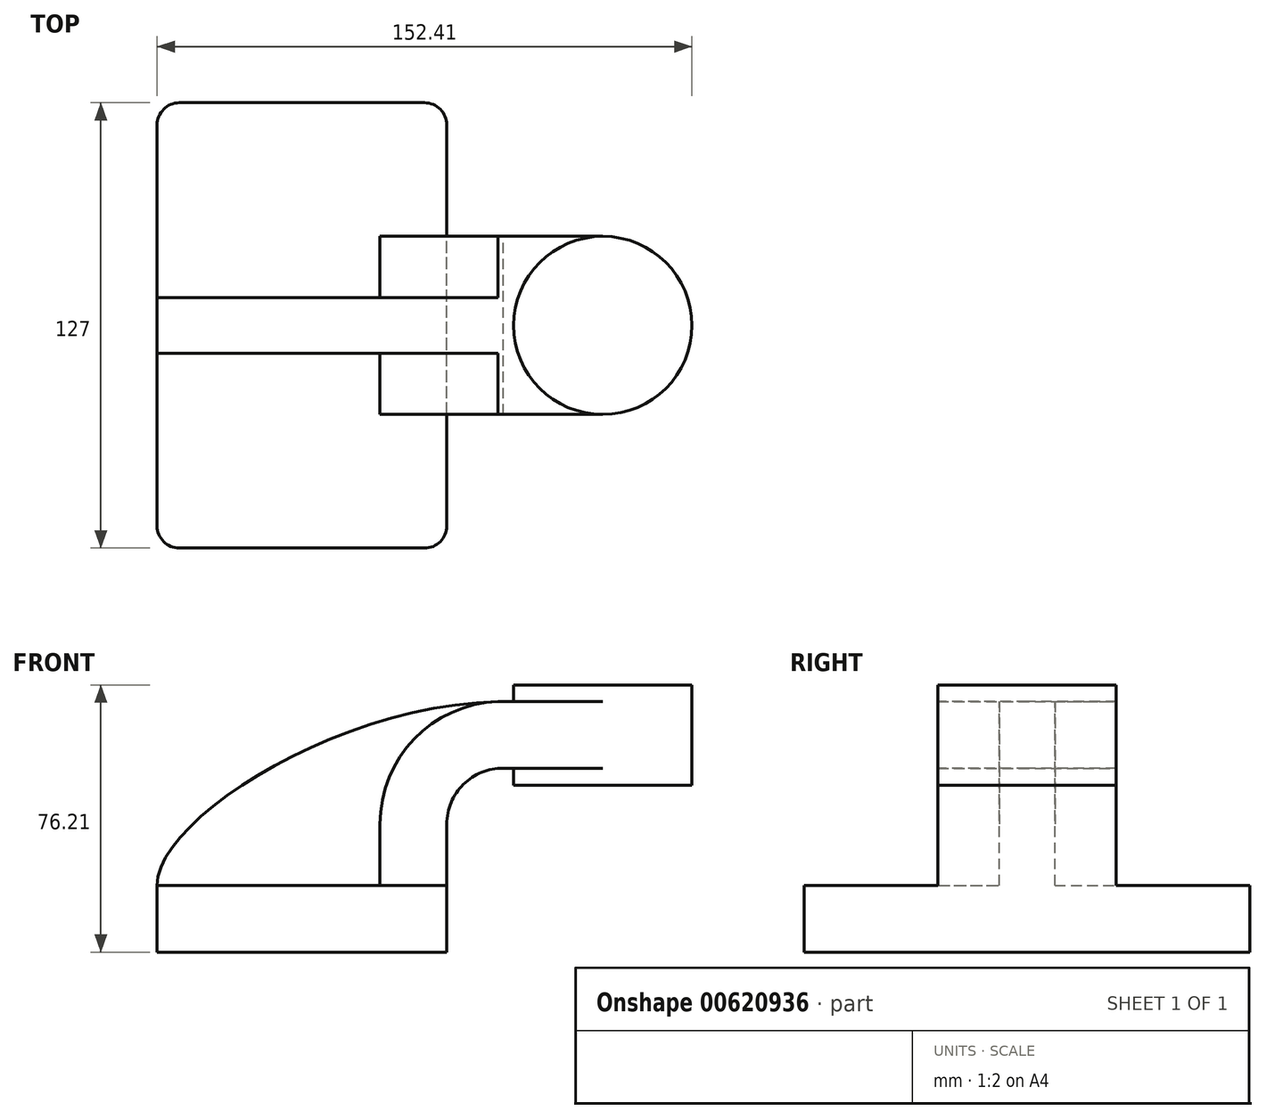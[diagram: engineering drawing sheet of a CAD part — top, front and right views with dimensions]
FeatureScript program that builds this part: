
annotation { "Feature Type Name" : "Feature", "Feature Type Description" : "" }
export const myFeature = defineFeature(function(context is Context, id is Id, definition is map)
    precondition{}
    {
        {
            var Q0;
            Q0=qCreatedBy(makeId("Front.planeOp"),FACE);
            var sketch = newSketch(context, id + "F0", { "sketchPlane" : qUnion([Q0])});
            skLineSegment(sketch, "E0.bottom", {"start": v(41.28, -9.52) * mm, "end": v(-41.28, -9.53) * mm});
            skLineSegment(sketch, "E0.top", {"start": v(41.27, 9.53) * mm, "end": v(-41.28, 9.53) * mm});
            skLineSegment(sketch, "E0.left", {"start": v(41.28, -9.52) * mm, "end": v(41.28, 9.53) * mm});
            skLineSegment(sketch, "E0.right", {"start": v(-41.28, -9.53) * mm, "end": v(-41.28, 9.53) * mm});
            skPoint(sketch, "E0.middle", {"position": v(0, 0) * mm});
            skLineSegment(sketch, "E1.bottom", {"start": v(111.12, 38.1) * mm, "end": v(60.32, 38.1) * mm});
            skLineSegment(sketch, "E1.top", {"start": v(111.12, 66.68) * mm, "end": v(60.32, 66.67) * mm});
            skLineSegment(sketch, "E1.left", {"start": v(111.12, 38.1) * mm, "end": v(111.12, 66.67) * mm});
            skLineSegment(sketch, "E1.right", {"start": v(60.32, 38.1) * mm, "end": v(60.32, 66.67) * mm});
            skPoint(sketch, "E1.middle", {"position": v(85.72, 52.39) * mm});
            skLineSegment(sketch, "E2", {"start": v(41.27, 9.53) * mm, "end": v(41.27, 27) * mm});
            skArc(sketch, "E3", {"start": v(41.27, 27) * mm, "mid": v(45.99, 38.3) * mm, "end": v(57.33, 42.88) * mm});
            skLineSegment(sketch, "E4", {"start": v(60.32, 38.1) * mm, "end": v(60.32, 38.1) * mm});
            skLineSegment(sketch, "E5", {"start": v(57.33, 42.88) * mm, "end": v(85.72, 42.88) * mm});
            skLineSegment(sketch, "E6.0", {"start": v(57.42, 61.93) * mm, "end": v(116.12, 61.93) * mm});
            skArc(sketch, "E6.1", {"start": v(22.23, 27) * mm, "mid": v(32.55, 51.8) * mm, "end": v(57.42, 61.93) * mm});
            skLineSegment(sketch, "E6.2", {"start": v(22.23, 9.53) * mm, "end": v(22.23, 27) * mm});
            skLineSegment(sketch, "E7", {"start": v(85.72, 38.1) * mm, "end": v(85.72, 66.67) * mm});
            skFitSpline(sketch, "E8", {"points": [v(-41.28, 9.53) * mm, v(57.42, 61.93) * mm], "startDerivative": vector(-0.5, 56.4) * mm, "endDerivative": vector(140.63, 0.96) * mm});
            skSolve(sketch);
        }
        {
            var Q0;
            Q0=makeQuery(id+"F0.imprint","IMPRINT",FACE,{"disambiguationData":[TD([[makeQuery(id+"F0.imprint","IMPRINT",EDGE,{"derivedFrom":sQuery(id+"F0.wireOp",EDGE,"E0.bottom")}),-1.0]])]});
            extrude(context, id + "F1", {"entities" : qUnion([Q0]), "endBound" : BoundingType.SYMMETRIC, "depth" : 127 * mm, "offsetDistance" : 25.4 * mm});
        }
        {
            var Q0;
            {var subQ1=sQuery(id+"F0.wireOp",EDGE,"E2");Q0=makeQuery(id+"F0.imprint","IMPRINT",FACE,{"disambiguationData":[TD([[makeQuery(id+"F0.imprint","IMPRINT",EDGE,{"derivedFrom":subQ1}),1.0]])]});}
            var Q1;
            {var subQ0=sQuery(id+"F0.wireOp",EDGE,"E5");var subQ1=sQuery(id+"F0.wireOp",EDGE,"E1.right");var subQ2=makeQuery(id+"F0.imprint","INTERSECT",VERTEX,{"derivedFrom":[subQ1,subQ0]});Q1=makeQuery(id+"F0.imprint","IMPRINT",FACE,{"disambiguationData":[TD([[makeQuery(id+"F0.imprint","IMPRINT",EDGE,{"disambiguationData":[TD([[subQ2,-1.0]])],"derivedFrom":subQ1}),-1.0]])]});}
            extrude(context, id + "F2", {"entities" : qUnion([Q0, Q1]), "operationType" : NewBodyOperationType.ADD, "endBound" : BoundingType.SYMMETRIC, "depth" : 50.8 * mm, "offsetDistance" : 25.4 * mm});
        }
        {
            var Q0;
            {var subQ3=sQuery(id+"F0.wireOp",EDGE,"E6.2");Q0=makeQuery(id+"F0.imprint","IMPRINT",FACE,{"disambiguationData":[TD([[makeQuery(id+"F0.imprint","IMPRINT",EDGE,{"derivedFrom":subQ3}),1.0]])]});}
            extrude(context, id + "F3", {"entities" : qUnion([Q0]), "operationType" : NewBodyOperationType.ADD, "endBound" : BoundingType.SYMMETRIC, "depth" : 15.88 * mm, "offsetDistance" : 25.4 * mm});
        }
        {
            var Q0;
            {var subQ0=sQuery(id+"F0.wireOp",EDGE,"E1.left");var subQ1=sQuery(id+"F0.wireOp",EDGE,"E1.top");var subQ2=makeQuery(id+"F0.imprint","INTERSECT",VERTEX,{"derivedFrom":[subQ1,subQ0]});Q0=makeQuery(id+"F0.imprint","IMPRINT",FACE,{"disambiguationData":[TD([[makeQuery(id+"F0.imprint","IMPRINT",EDGE,{"disambiguationData":[TD([[subQ2,-1.0]])],"derivedFrom":subQ1}),1.0]])]});}
            var Q1;
            {var subQ2=sQuery(id+"F0.wireOp",EDGE,"E1.bottom");var subQ4=sQuery(id+"F0.wireOp",EDGE,"E1.left");var subQ5=makeQuery(id+"F0.imprint","INTERSECT",VERTEX,{"derivedFrom":[subQ2,subQ4]});Q1=makeQuery(id+"F0.imprint","IMPRINT",FACE,{"disambiguationData":[TD([[makeQuery(id+"F0.imprint","IMPRINT",EDGE,{"disambiguationData":[TD([[subQ5,-1.0]])],"derivedFrom":subQ2}),-1.0]])]});}
            var Q2;
            Q2=sQuery(id+"F0.wireOp",EDGE,"E7");
            revolve(context, id + "F4", {"operationType" : NewBodyOperationType.ADD, "entities" : qUnion([Q0, Q1]), "axis" : qUnion([Q2]), "revolveType" : RevolveType.FULL});
        }
        {
            var Q0;
            Q0=makeQuery(id+"F1.opExtrude","CAP_EDGE",EDGE,{"disambiguationData":[OSD([sQuery(id+"F0.wireOp",EDGE,"E0.right")])],"isStart":false});
            var Q1;
            Q1=makeQuery(id+"F1.opExtrude","CAP_EDGE",EDGE,{"disambiguationData":[OSD([sQuery(id+"F0.wireOp",EDGE,"E0.left")])],"isStart":false});
            var Q2;
            Q2=makeQuery(id+"F1.opExtrude","CAP_EDGE",EDGE,{"disambiguationData":[OSD([sQuery(id+"F0.wireOp",EDGE,"E0.left")])],"isStart":true});
            var Q3;
            Q3=makeQuery(id+"F1.opExtrude","CAP_EDGE",EDGE,{"disambiguationData":[OSD([sQuery(id+"F0.wireOp",EDGE,"E0.right")])],"isStart":true});
            fillet(context, id + "F5", {"entities" : qUnion([Q0, Q1, Q2, Q3]), "radius" : 6.35 * mm, "tangentPropagation" : true, "allowEdgeOverflow" : false});
        }
    });
